# Revit family: 1632 Haiku 2 Seater
name_source: partatom
category: Furniture
revit_build: Autodesk Revit 2017 (Build: 20171027_0315(x64)
units: mm (PartAtom-declared; Revit-internal decimal feet)

## family parameters
Always vertical = Yes
Cut with Voids When Loaded = No
OmniClass Number = 23.40.20.00
OmniClass Title = General Furniture and Specialties
Room Calculation Point = No
Shared = No
Work Plane-Based = No

## types (1)
- 1632 Haiku 2 Seater
    Back Cushion = FF Hallingdal 130
    Depth = 88 cm
    Description = x
    Design year = 2012
    Designer = Gamfratesi
    Height = 104 cm
    Item No. = 1632
    Legs = FF Black Metal
    Manufacturer = Fredericia Furniture
    Model = 1632 Haiku 2 Seater
    Seat Cushion = FF Hallingdal 130
    Seat Height = 44,5 cm
    Shell Modify = Change Shell Material in Mange -> Object Styles->Imported objects
    URL = https://www.fredericia.com
    Variation Legs = Avaible in black metal
    Variations Upholster = Available in fabric or leather
    Weight = 56 kg
    Width = 156 cm

## geometry (parser evidence)
native form markers: Sweep x3
no freeform markers — native parametric forms only
